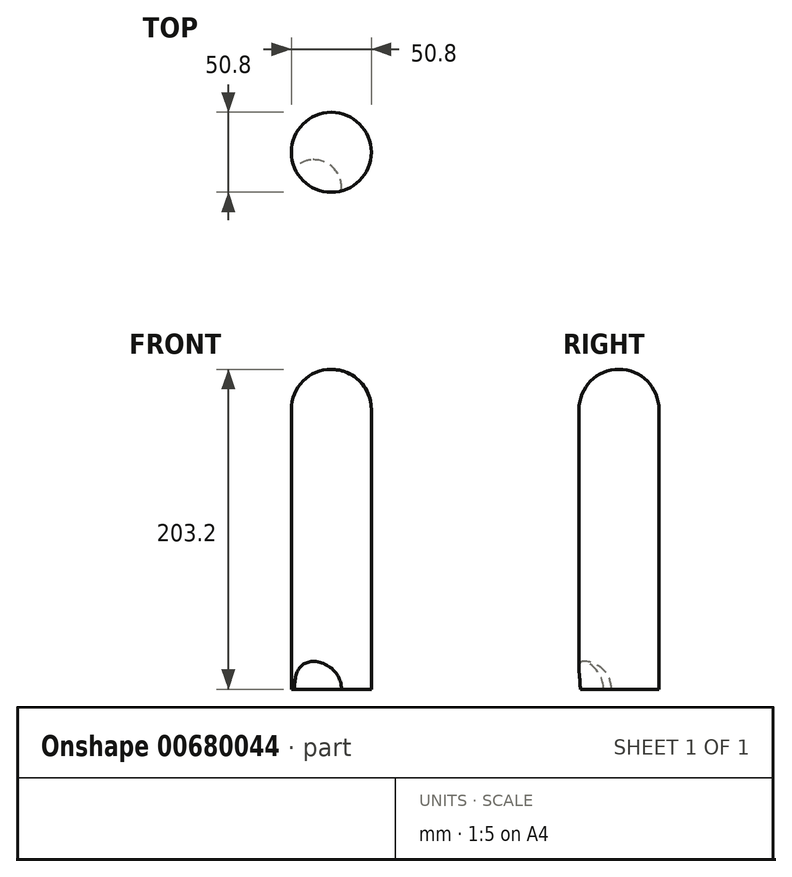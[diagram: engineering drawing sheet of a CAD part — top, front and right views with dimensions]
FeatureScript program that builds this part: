
annotation { "Feature Type Name" : "Feature", "Feature Type Description" : "" }
export const myFeature = defineFeature(function(context is Context, id is Id, definition is map)
    precondition{}
    {
        {
            var Q0;
            Q0=qCreatedBy(makeId("Top.planeOp"),FACE);
            var sketch = newSketch(context, id + "F0", { "sketchPlane" : qUnion([Q0])});
            skCircle(sketch, "E0", {"center": v(0, 0) * mm, "radius": 25.4 * mm});
            skSolve(sketch);
        }
        {
            var Q0;
            Q0=makeQuery(id+"F0.imprint","IMPRINT",FACE,{"disambiguationData":[TD([[makeQuery(id+"F0.imprint","IMPRINT",EDGE,{"derivedFrom":sQuery(id+"F0.wireOp",EDGE,"E0")}),1.0]])]});
            extrude(context, id + "F1", {"entities" : qUnion([Q0]), "depth" : 203.2 * mm, "offsetDistance" : 25.4 * mm});
        }
        {
            var Q0;
            Q0=makeQuery(id+"F1.opExtrude","CAP_EDGE",EDGE,{"disambiguationData":[OSD([sQuery(id+"F0.wireOp",EDGE,"E0")])],"isStart":false});
            fillet(context, id + "F2", {"entities" : qUnion([Q0]), "radius" : 25.4 * mm, "tangentPropagation" : true, "allowEdgeOverflow" : false});
        }
        {
            var Q0;
            Q0=qCreatedBy(makeId("Top.planeOp"),FACE);
            var sketch = newSketch(context, id + "F3", { "sketchPlane" : qUnion([Q0])});
            skCircle(sketch, "E1", {"center": v(-11.11, -22.44) * mm, "radius": 17.68 * mm});
            skLineSegment(sketch, "E2", {"start": v(-12.85, -4.85) * mm, "end": v(-11.11, -22.44) * mm});
            skLineSegment(sketch, "E3", {"start": v(-12.85, -4.85) * mm, "end": v(-9.37, -40.03) * mm});
            skSolve(sketch);
        }
        {
            var Q0;
            {var subQ0=sQuery(id+"F3.wireOp",EDGE,"E3");var subQ4=makeQuery(id+"F3.imprint","IMPRINT",VERTEX,{"derivedFrom":subQ0});Q0=makeQuery(id+"F3.imprint","IMPRINT",FACE,{"disambiguationData":[TD([[makeQuery(id+"F3.imprint","IMPRINT",EDGE,{"disambiguationData":[TD([[subQ4,1.0]])],"derivedFrom":subQ0}),-1.0]])]});}
            var Q1;
            Q1=sQuery(id+"F3.wireOp",EDGE,"E3");
            revolve(context, id + "F4", {"operationType" : NewBodyOperationType.ADD, "entities" : qUnion([Q0]), "axis" : qUnion([Q1]), "revolveType" : RevolveType.FULL});
        }
    });
